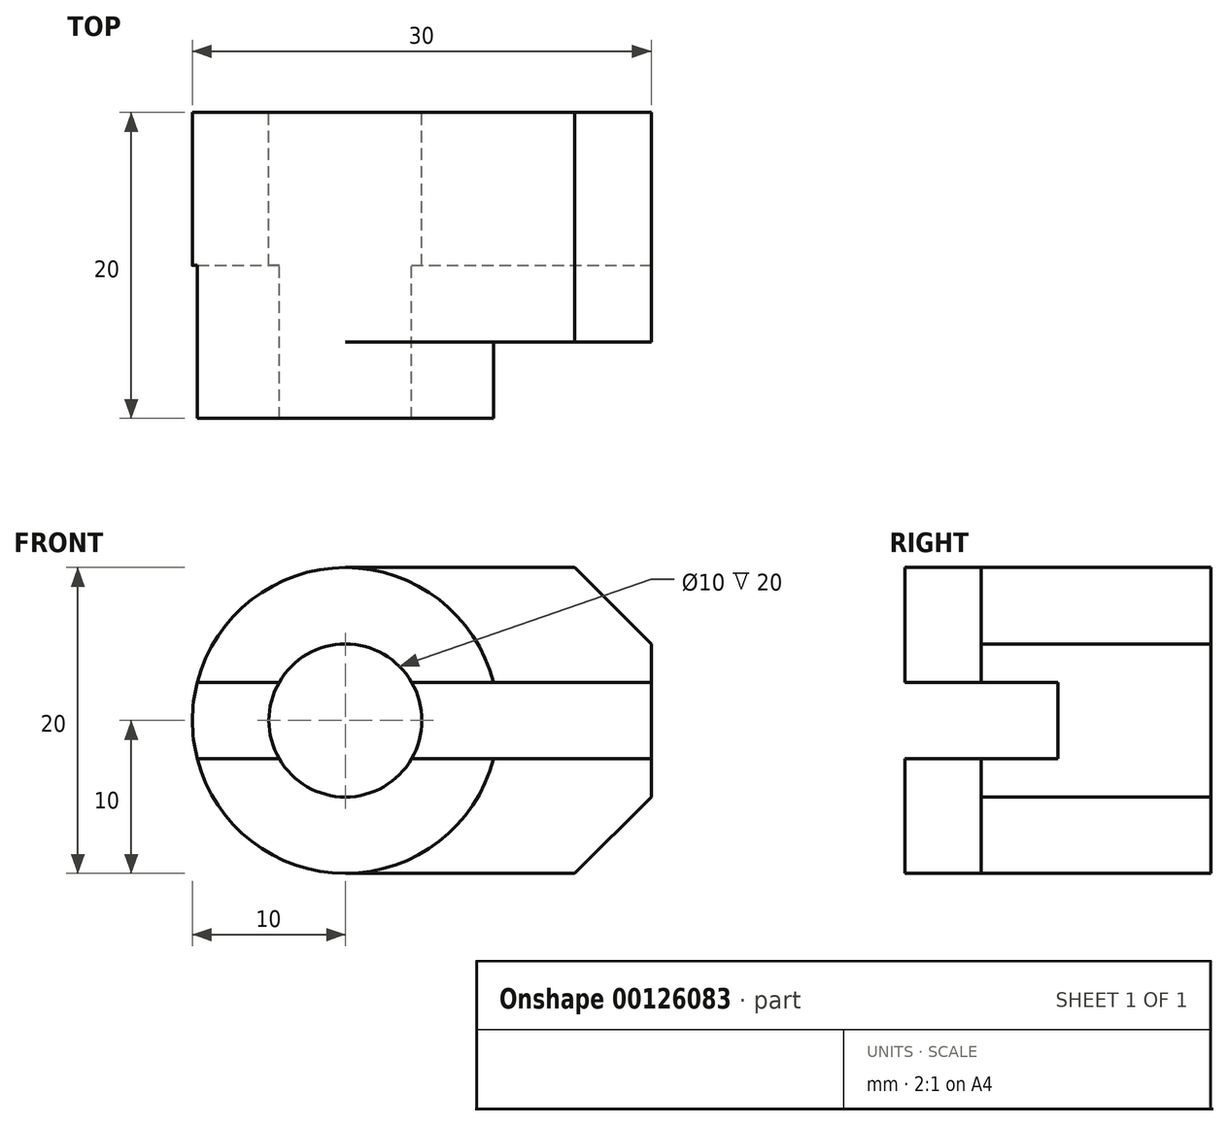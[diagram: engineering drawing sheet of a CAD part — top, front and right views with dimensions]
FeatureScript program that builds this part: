
annotation { "Feature Type Name" : "Feature", "Feature Type Description" : "" }
export const myFeature = defineFeature(function(context is Context, id is Id, definition is map)
    precondition{}
    {
        {
            var Q0;
            Q0=qCreatedBy(makeId("Front.planeOp"),FACE);
            var sketch = newSketch(context, id + "F0", { "sketchPlane" : qUnion([Q0])});
            skCircle(sketch, "E0", {"center": v(0, 0) * mm, "radius": 5 * mm});
            skCircle(sketch, "E1", {"center": v(0, 0) * mm, "radius": 10 * mm});
            skSolve(sketch);
        }
        {
            var Q0;
            Q0 = qSketchRegion(id + "F0", true);
            extrude(context, id + "F1", {"entities" : qUnion([Q0]), "endBound" : BoundingType.SYMMETRIC, "depth" : 20 * mm});
        }
        {
            var Q0;
            Q0=makeQuery(id+"F1.opExtrude","CAP_FACE",FACE,{"disambiguationData":[OSD([sQuery(id+"F0.wireOp",EDGE,"E0"),sQuery(id+"F0.wireOp",EDGE,"E1")])],"isStart":true});
            var sketch = newSketch(context, id + "F2", { "sketchPlane" : qUnion([Q0])});
            skLineSegment(sketch, "E2", {"start": v(0, 0) * mm, "end": v(0, 10) * mm});
            skLineSegment(sketch, "E3", {"start": v(0, 10) * mm, "end": v(-15, 10) * mm});
            skLineSegment(sketch, "E4", {"start": v(-15, -10) * mm, "end": v(0, -10) * mm});
            skLineSegment(sketch, "E5", {"start": v(0, -10) * mm, "end": v(0, 0) * mm});
            skLineSegment(sketch, "E6", {"start": v(-15, 10) * mm, "end": v(-20, 5) * mm});
            skLineSegment(sketch, "E7", {"start": v(-15, -10) * mm, "end": v(-20, -5) * mm});
            skLineSegment(sketch, "E8", {"start": v(-20, 5) * mm, "end": v(-20, -5) * mm});
            skSolve(sketch);
        }
        {
            var Q0;
            Q0 = qSketchRegion(id + "F2", true);
            extrude(context, id + "F3", {"entities" : qUnion([Q0]), "operationType" : NewBodyOperationType.ADD, "oppositeDirection" : true, "depth" : 15 * mm});
        }
        {
            var Q0;
            Q0=makeQuery(id+"F0.imprint","IMPRINT",FACE,{"disambiguationData":[TD([[makeQuery(id+"F0.imprint","IMPRINT",EDGE,{"derivedFrom":sQuery(id+"F0.wireOp",EDGE,"E0")}),1.0]])]});
            extrude(context, id + "F4", {"entities" : qUnion([Q0]), "operationType" : NewBodyOperationType.REMOVE, "endBound" : BoundingType.SYMMETRIC, "oppositeDirection" : true, "depth" : 20 * mm});
        }
        {
            var Q0;
            Q0=qCreatedBy(makeId("Front.planeOp"),FACE);
            var sketch = newSketch(context, id + "F5", { "sketchPlane" : qUnion([Q0])});
            skLineSegment(sketch, "E9", {"start": v(0, 2.5) * mm, "end": v(-10, 2.5) * mm});
            skLineSegment(sketch, "E10", {"start": v(-10, 2.5) * mm, "end": v(-10, -2.5) * mm});
            skLineSegment(sketch, "E11", {"start": v(-10, -2.5) * mm, "end": v(20, -2.5) * mm});
            skLineSegment(sketch, "E12", {"start": v(0, 2.5) * mm, "end": v(20, 2.5) * mm});
            skLineSegment(sketch, "E13", {"start": v(20, 2.5) * mm, "end": v(20, -2.5) * mm});
            skSolve(sketch);
        }
        {
            var Q0;
            Q0 = qSketchRegion(id + "F5", true);
            var Q1;
            Q1=makeQuery(id+"F1.opExtrude","CAP_FACE",FACE,{"disambiguationData":[OSD([sQuery(id+"F0.wireOp",EDGE,"E0"),sQuery(id+"F0.wireOp",EDGE,"E1")])],"isStart":false});
            extrude(context, id + "F6", {"entities" : qUnion([Q0]), "operationType" : NewBodyOperationType.REMOVE, "endBound" : BoundingType.UP_TO_SURFACE, "endBoundEntityFace" : qUnion([Q1]), "depth" : 25 * mm});
        }
    });
